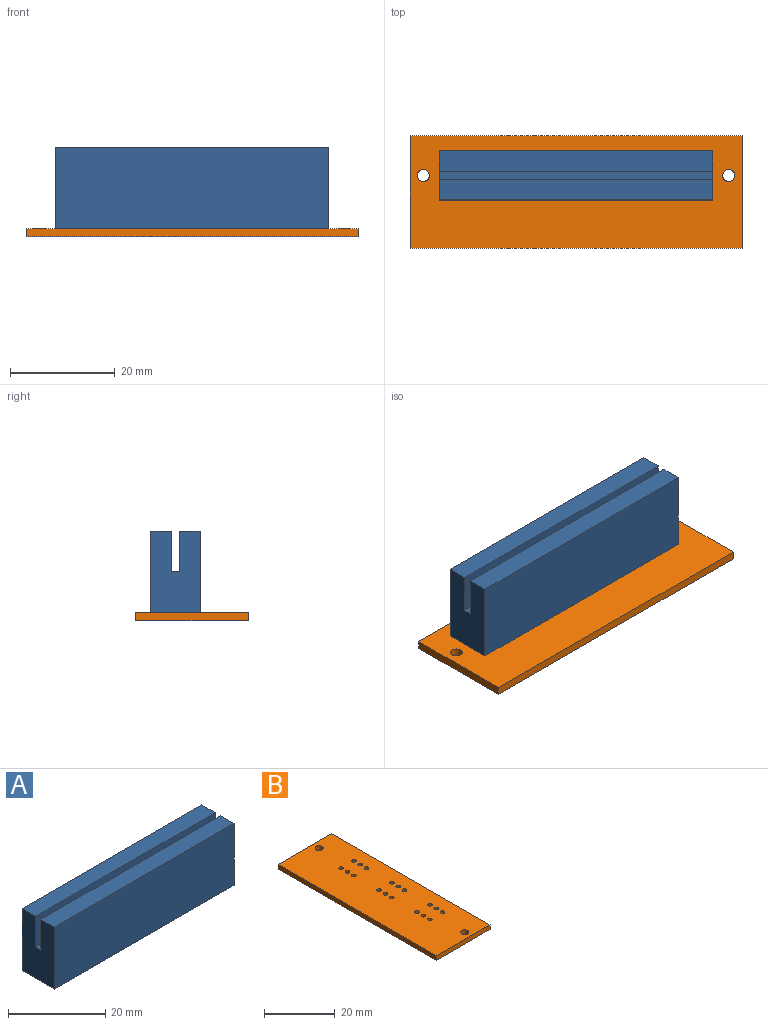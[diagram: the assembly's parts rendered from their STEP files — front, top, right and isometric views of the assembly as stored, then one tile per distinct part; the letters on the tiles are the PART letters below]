
ASSEMBLY  parts=2 mates=1
PART A: 10 faces, bbox 52.3x9.4x15.6 mm
  f0: plane 52.32x3.92mm, normal (0,0,1), area 205.3mm2, adj f1,f2,f3,f7
  f1: plane 15.6x9.4mm, normal (1,0,0), area 134.7mm2, adj f0,f2,f4,f5,f6,f7,f8,f9
  f2: plane 52.32x15.6mm, normal (0,1,0), area 816.3mm2, adj f0,f1,f3,f6
  f3: plane 15.6x9.4mm, normal (-1,0,0), area 134.7mm2, adj f0,f2,f4,f5,f6,f7,f8,f9
  f4: plane 52.32x15.6mm, normal (0,-1,0), area 816.3mm2, adj f1,f3,f5,f6
  f5: plane 52.32x3.92mm, normal (0,0,1), area 205.3mm2, adj f1,f3,f4,f8
  f6: plane 52.32x9.4mm, normal (0,0,-1), area 491.7mm2, adj f1,f2,f3,f4
  f7: plane 52.32x7.7mm, normal (0,-1,0), area 402.9mm2, adj f0,f1,f3,f9
  f8: plane 52.32x7.7mm, normal (0,1,0), area 402.9mm2, adj f1,f3,f5,f9
  f9: plane 52.32x1.55mm, normal (0,0,1), area 81.1mm2, adj f1,f3,f7,f8
PART B: 26 faces, bbox 21.6x63.5x1.6 mm
  f0: plane 21.56x1.6mm, normal (0,-1,0), area 34.5mm2, adj f1,f23,f24,f25
  f1: plane 63.5x1.6mm, normal (1,0,0), area 101.6mm2, adj f0,f2,f24,f25
  f2: plane 21.56x1.6mm, normal (0,1,0), area 34.5mm2, adj f1,f23,f24,f25
  f3: cylinder r=1.14mm len=2.29mm, axis (0,0,-1), area 11.5mm2, adj f24,f25
  f4: cylinder r=1.14mm len=2.29mm, axis (0,0,-1), area 11.5mm2, adj f24,f25
  f5: cylinder r=0.64mm len=1.6mm, axis (0,0,-1), area 6.4mm2, adj f24,f25
  f6: cylinder r=0.64mm len=1.6mm, axis (0,0,-1), area 6.4mm2, adj f24,f25
  f7: cylinder r=0.64mm len=1.6mm, axis (0,0,-1), area 6.4mm2, adj f24,f25
  f8: cylinder r=0.64mm len=1.6mm, axis (0,0,-1), area 6.4mm2, adj f24,f25
  f9: cylinder r=0.64mm len=1.6mm, axis (0,0,-1), area 6.4mm2, adj f24,f25
  f10: cylinder r=0.64mm len=1.6mm, axis (0,0,-1), area 6.4mm2, adj f24,f25
  f11: cylinder r=0.64mm len=1.6mm, axis (0,0,-1), area 6.4mm2, adj f24,f25
  f12: cylinder r=0.64mm len=1.6mm, axis (0,0,-1), area 6.4mm2, adj f24,f25
  f13: cylinder r=0.64mm len=1.6mm, axis (0,0,-1), area 6.4mm2, adj f24,f25
  f14: cylinder r=0.64mm len=1.6mm, axis (0,0,-1), area 6.4mm2, adj f24,f25
  f15: cylinder r=0.64mm len=1.6mm, axis (0,0,-1), area 6.4mm2, adj f24,f25
  f16: cylinder r=0.64mm len=1.6mm, axis (0,0,-1), area 6.4mm2, adj f24,f25
  f17: cylinder r=0.64mm len=1.6mm, axis (0,0,-1), area 6.4mm2, adj f24,f25
  f18: cylinder r=0.64mm len=1.6mm, axis (0,0,-1), area 6.4mm2, adj f24,f25
  f19: cylinder r=0.64mm len=1.6mm, axis (0,0,-1), area 6.4mm2, adj f24,f25
  f20: cylinder r=0.64mm len=1.6mm, axis (0,0,-1), area 6.4mm2, adj f24,f25
  f21: cylinder r=0.64mm len=1.6mm, axis (0,0,-1), area 6.4mm2, adj f24,f25
  f22: cylinder r=0.64mm len=1.6mm, axis (0,0,-1), area 6.4mm2, adj f24,f25
  f23: plane 63.5x1.6mm, normal (-1,0,0), area 101.6mm2, adj f0,f2,f24,f25
  f24: plane 63.5x21.56mm, normal (0,0,1), area 1338mm2, adj f0,f1,f2,f3,f4,f5,f6,f7
  f25: plane 63.5x21.56mm, normal (0,0,-1), area 1338mm2, adj f0,f1,f2,f3,f4,f5,f6,f7
PLACE A t=(-4.43,-16.61,5.57)mm
PLACE B rot(axis=(0.71,0.71,0),180deg) t=(-62.35,-4.29,5.57)mm
MATE fastened A.f6 <-> B.f25  axis (0,0,-1) through (-30.6,-7.21,5.57)mm
